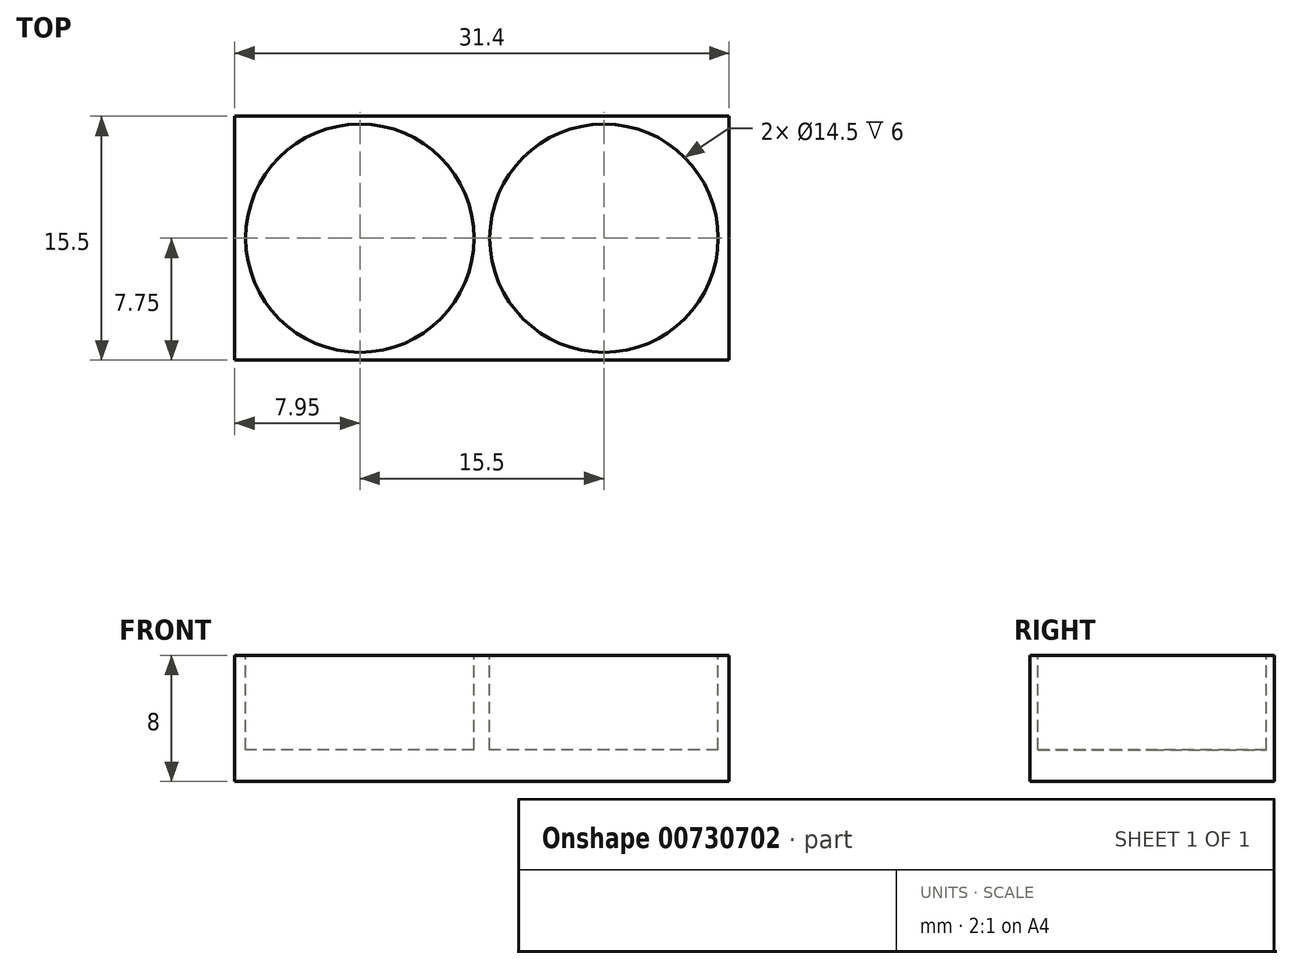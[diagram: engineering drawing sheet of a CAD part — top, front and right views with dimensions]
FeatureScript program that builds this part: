
annotation { "Feature Type Name" : "Feature", "Feature Type Description" : "" }
export const myFeature = defineFeature(function(context is Context, id is Id, definition is map)
    precondition{}
    {
        {
            assignVariable(context, id + "F0", {"name" : "height", "anyValue" : 8 * mm});
        }
        {
            assignVariable(context, id + "F1", {"name" : "depth", "anyValue" : 6 * mm});
        }
        {
            var Q0;
            Q0=qCreatedBy(makeId("Top.planeOp"),FACE);
            var sketch = newSketch(context, id + "F2", { "sketchPlane" : qUnion([Q0])});
            skLineSegment(sketch, "E0.bottom", {"start": v(15.7, -7.75) * mm, "end": v(-15.7, -7.75) * mm});
            skLineSegment(sketch, "E0.top", {"start": v(15.7, 7.75) * mm, "end": v(-15.7, 7.75) * mm});
            skLineSegment(sketch, "E0.left", {"start": v(15.7, -7.75) * mm, "end": v(15.7, 7.75) * mm});
            skLineSegment(sketch, "E0.right", {"start": v(-15.7, -7.75) * mm, "end": v(-15.7, 7.75) * mm});
            skPoint(sketch, "E0.middle", {"position": v(0, 0) * mm});
            skSolve(sketch);
        }
        {
            var Q0;
            Q0=makeQuery(id+"F2.imprint","IMPRINT",FACE,{"disambiguationData":[TD([[makeQuery(id+"F2.imprint","IMPRINT",EDGE,{"derivedFrom":sQuery(id+"F2.wireOp",EDGE,"E0.bottom")}),-1.0]])]});
            var Q1;
            Q1=makeQuery(id+"F2.imprint","IMPRINT",FACE,{"disambiguationData":[TD([[makeQuery(id+"F2.imprint","IMPRINT",EDGE,{"derivedFrom":sQuery(id+"F2.wireOp",EDGE,"dZZn7ktD-icDM-W65f-fWEV-sYn1Fpl9ZXgg")}),1.0]])]});
            var Q2;
            Q2=makeQuery(id+"F2.imprint","IMPRINT",FACE,{"disambiguationData":[TD([[makeQuery(id+"F2.imprint","IMPRINT",EDGE,{"derivedFrom":sQuery(id+"F2.wireOp",EDGE,"wgxVGCNF-AMx4-EwNK-9CKD-N2RlzXdfOdLf")}),1.0]])]});
            extrude(context, id + "F3", {"entities" : qUnion([Q0, Q1, Q2]), "depth" : getVariable(context, 'height'), "offsetDistance" : 25 * mm});
        }
        {
            var Q0;
            Q0=makeQuery(id+"F3.opExtrude","CAP_FACE",FACE,{"disambiguationData":[OSD([sQuery(id+"F2.wireOp",EDGE,"E0.bottom"),sQuery(id+"F2.wireOp",EDGE,"E0.top"),sQuery(id+"F2.wireOp",EDGE,"E0.left"),sQuery(id+"F2.wireOp",EDGE,"E0.right")])],"isStart":false});
            var sketch = newSketch(context, id + "F4", { "sketchPlane" : qUnion([Q0])});
            skLineSegment(sketch, "E1", {"start": v(0, 0) * mm, "end": v(7.75, 0) * mm, "construction": true});
            skLineSegment(sketch, "E2", {"start": v(0, 0) * mm, "end": v(-7.75, 0) * mm, "construction": true});
            skCircle(sketch, "E3", {"center": v(-7.75, 0) * mm, "radius": 7.25 * mm});
            skCircle(sketch, "E4", {"center": v(7.75, 0) * mm, "radius": 7.25 * mm});
            skSolve(sketch);
        }
        {
            var Q0;
            Q0=makeQuery(id+"F4.imprint","IMPRINT",FACE,{"disambiguationData":[TD([[makeQuery(id+"F4.imprint","IMPRINT",EDGE,{"derivedFrom":sQuery(id+"F4.wireOp",EDGE,"E3")}),1.0]])]});
            var Q1;
            Q1=makeQuery(id+"F4.imprint","IMPRINT",FACE,{"disambiguationData":[TD([[makeQuery(id+"F4.imprint","IMPRINT",EDGE,{"derivedFrom":sQuery(id+"F4.wireOp",EDGE,"E4")}),1.0]])]});
            extrude(context, id + "F5", {"entities" : qUnion([Q0, Q1]), "operationType" : NewBodyOperationType.REMOVE, "oppositeDirection" : true, "depth" : getVariable(context, 'depth'), "offsetDistance" : 25 * mm});
        }
    });
